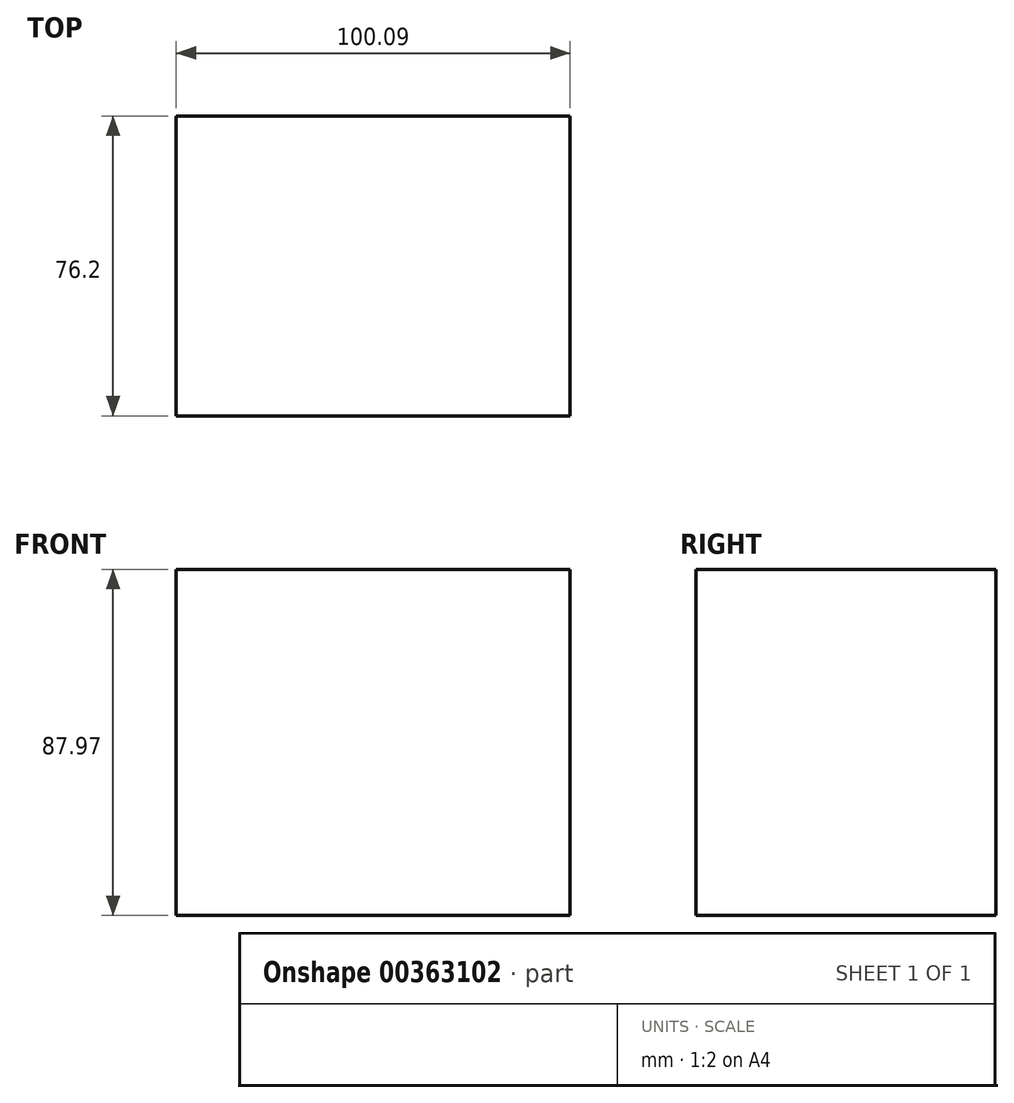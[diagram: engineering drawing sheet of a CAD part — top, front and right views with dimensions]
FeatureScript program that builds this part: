
annotation { "Feature Type Name" : "Feature", "Feature Type Description" : "" }
export const myFeature = defineFeature(function(context is Context, id is Id, definition is map)
    precondition{}
    {
        {
            var Q0;
            Q0=qCreatedBy(makeId("Front.planeOp"),FACE);
            var sketch = newSketch(context, id + "F0", { "sketchPlane" : qUnion([Q0])});
            skLineSegment(sketch, "E0.bottom", {"start": v(-53.23, 47.81) * mm, "end": v(46.86, 47.81) * mm});
            skLineSegment(sketch, "E0.top", {"start": v(-53.23, -40.16) * mm, "end": v(46.86, -40.16) * mm});
            skLineSegment(sketch, "E0.left", {"start": v(-53.23, 47.81) * mm, "end": v(-53.23, -40.16) * mm});
            skLineSegment(sketch, "E0.right", {"start": v(46.86, 47.81) * mm, "end": v(46.86, -40.16) * mm});
            skSolve(sketch);
        }
        {
            var Q0;
            Q0=makeQuery(id+"F0.imprint","IMPRINT",FACE,{"disambiguationData":[TD([[makeQuery(id+"F0.imprint","IMPRINT",EDGE,{"derivedFrom":sQuery(id+"F0.wireOp",EDGE,"E0.bottom")}),-1.0]])]});
            extrude(context, id + "F1", {"entities" : qUnion([Q0]), "depth" : 76.2 * mm});
        }
    });
